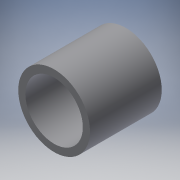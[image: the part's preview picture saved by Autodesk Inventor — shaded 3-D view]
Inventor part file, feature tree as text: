
AUTODESK INVENTOR PART (.ipt)
format: ipt  version: 2018.2 (Build 222227000, 227)  size: 100,864 bytes
history: native  units: mm
features: other x1, extrude x1, sketch x1
ambient origin geometry x8: Origin, YZ Plane, XZ Plane, XY Plane, X Axis, Y Axis, Z Axis, Center Point
bodies: Body1 (feature_tree)
feature tree (3):
  other  "ソリッド1"
  extrude  "押し出し1"  Depth=10.0mm
  sketch  "スケッチ1"
